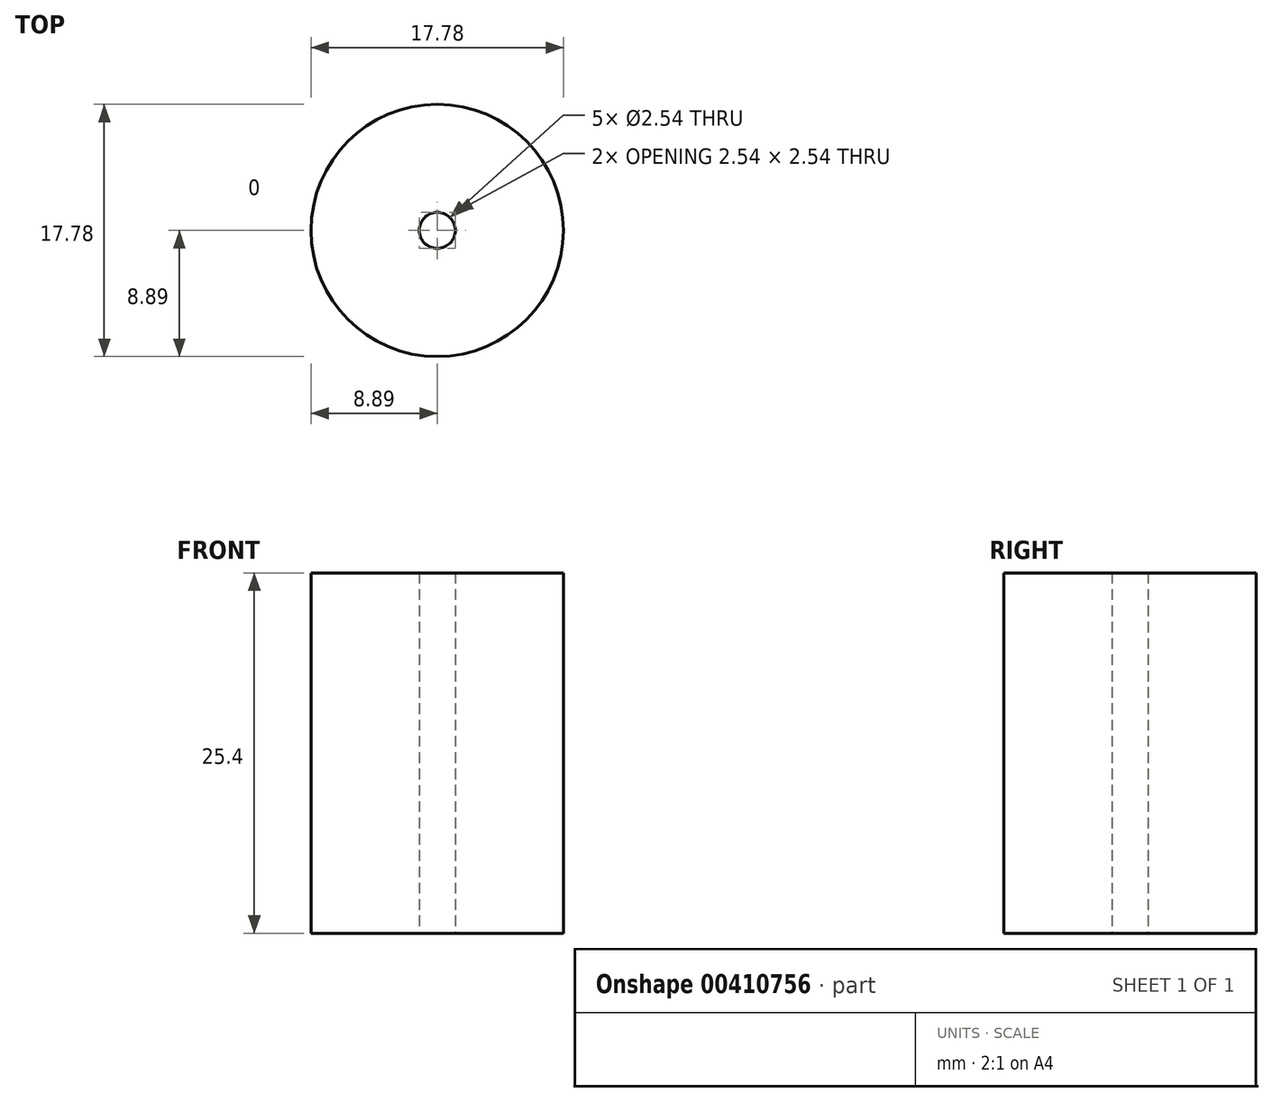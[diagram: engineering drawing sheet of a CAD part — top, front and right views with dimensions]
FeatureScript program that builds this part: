
annotation { "Feature Type Name" : "Feature", "Feature Type Description" : "" }
export const myFeature = defineFeature(function(context is Context, id is Id, definition is map)
    precondition{}
    {
        {
            var Q0;
            Q0=qCreatedBy(makeId("Top.planeOp"),FACE);
            var sketch = newSketch(context, id + "F0", { "sketchPlane" : qUnion([Q0])});
            skCircle(sketch, "E0", {"center": v(0, 0) * mm, "radius": 8.89 * mm});
            skSolve(sketch);
        }
        {
            var Q0;
            Q0=makeQuery(id+"F0.imprint","IMPRINT",FACE,{"disambiguationData":[TD([[makeQuery(id+"F0.imprint","IMPRINT",EDGE,{"derivedFrom":sQuery(id+"F0.wireOp",EDGE,"E0")}),1.0]])]});
            extrude(context, id + "F1", {"entities" : qUnion([Q0]), "depth" : 25.4 * mm});
        }
        {
            var Q0;
            Q0=sQuery(id+"F0.wireOp",VERTEX,"E0.center");
            var Q1;
            Q1=makeQuery(id+"F1.opExtrude","SWEPT_BODY",BODY,{"disambiguationData":[OSD([sQuery(id+"F0.wireOp",EDGE,"E0")])]});
            hole(context, id + "F2", {"style" : HoleStyle.SIMPLE, "endStyle" : HoleEndStyle.THROUGH, "oppositeDirection" : true, "holeDiameter" : 2.54 * mm, "isTappedThrough" : true, "tappedDepth" : 12.7 * mm, "tapClearance" : 3, "locations" : qUnion([Q0]), "scope" : qUnion([Q1])});
        }
    });
